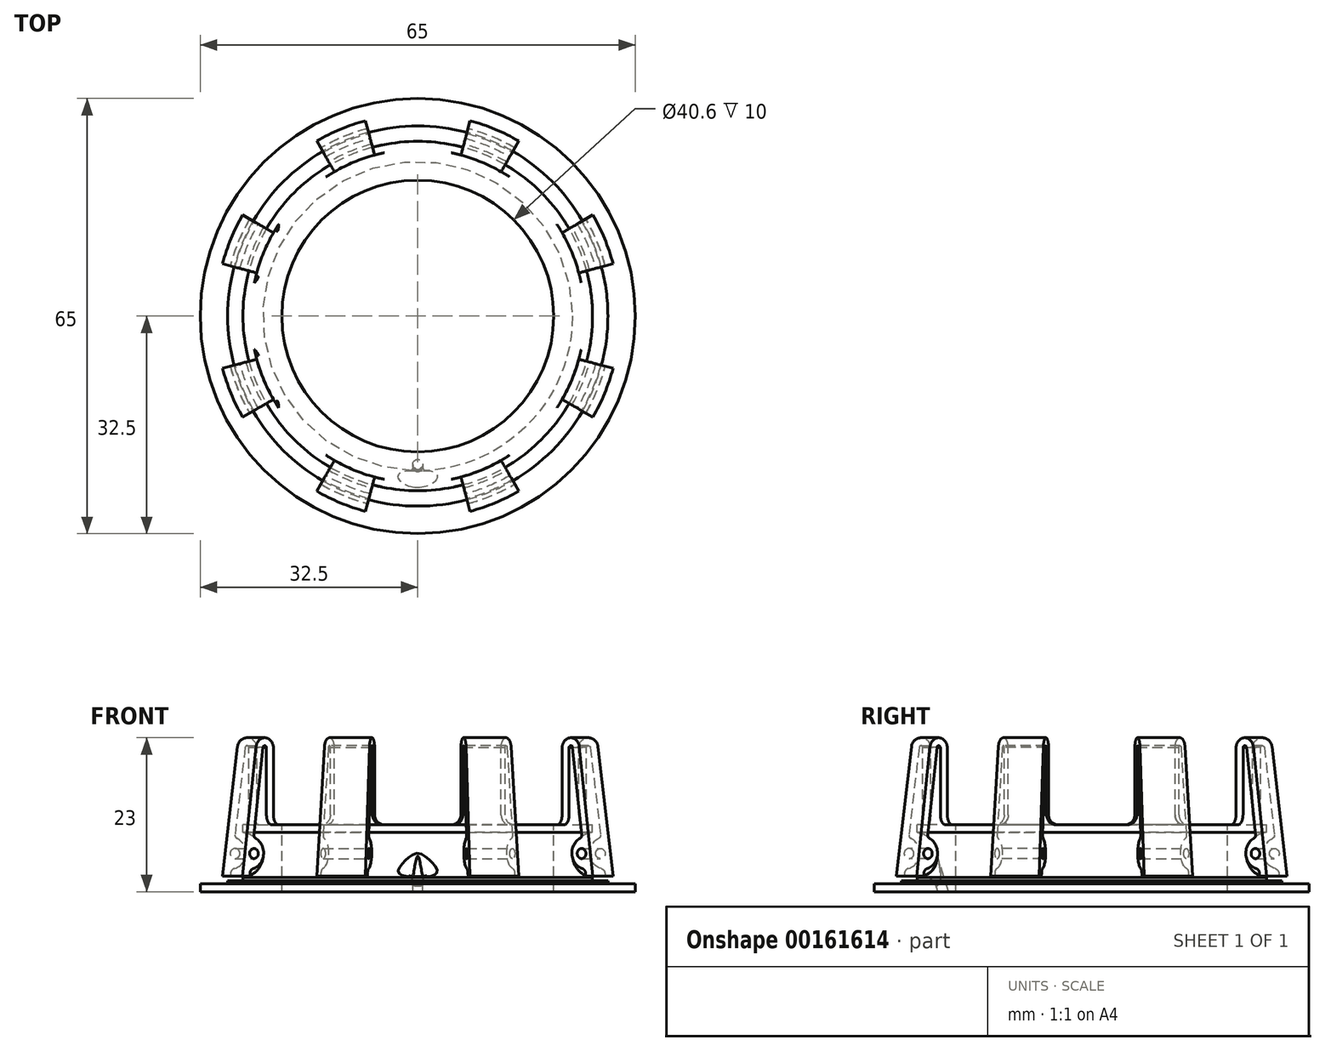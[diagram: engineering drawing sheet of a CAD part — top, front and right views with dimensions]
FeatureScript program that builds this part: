
annotation { "Feature Type Name" : "Feature", "Feature Type Description" : "" }
export const myFeature = defineFeature(function(context is Context, id is Id, definition is map)
    precondition{}
    {
        {
            var Q0;
            Q0=qCreatedBy(makeId("Front.planeOp"),FACE);
            var sketch = newSketch(context, id + "F0", { "sketchPlane" : qUnion([Q0])});
            skLineSegment(sketch, "E0", {"start": v(-32.5, 1.2) * mm, "end": v(-32.5, 0) * mm});
            skLineSegment(sketch, "E1", {"start": v(-32.5, 0) * mm, "end": v(-20.3, 0) * mm});
            skLineSegment(sketch, "E2", {"start": v(-32.5, 1.2) * mm, "end": v(-28.4, 1.2) * mm});
            skLineSegment(sketch, "E3", {"start": v(-28.4, 1.6) * mm, "end": v(-26.1, 1.6) * mm});
            skLineSegment(sketch, "E4", {"start": v(-20.3, 10) * mm, "end": v(-20.3, 0) * mm});
            skLineSegment(sketch, "E5", {"start": v(-20.3, 10) * mm, "end": v(0, 10) * mm, "construction": true});
            skLineSegment(sketch, "E6", {"start": v(0, 10) * mm, "end": v(0, 0) * mm, "construction": true});
            skLineSegment(sketch, "E7", {"start": v(0, 0) * mm, "end": v(-20.3, 0) * mm, "construction": true});
            skLineSegment(sketch, "E8", {"start": v(-29, 2.3) * mm, "end": v(-30.2, 2.3) * mm});
            skLineSegment(sketch, "E9", {"start": v(-30.2, 2.3) * mm, "end": v(-27.87, 21.69) * mm});
            skLineSegment(sketch, "E10", {"start": v(-29, 2.3) * mm, "end": v(-28.87, 3.4) * mm});
            skLineSegment(sketch, "E11", {"start": v(-26.1, 8.87) * mm, "end": v(-26.1, 21.58) * mm});
            skArc(sketch, "E12", {"start": v(-26.1, 21.58) * mm, "mid": v(-26.4, 21.8) * mm, "end": v(-26.69, 21.54) * mm});
            skLineSegment(sketch, "E13", {"start": v(-20.3, 10) * mm, "end": v(-24.9, 10) * mm});
            skLineSegment(sketch, "E14", {"start": v(-24.9, 10) * mm, "end": v(-24.9, 21.5) * mm});
            skArc(sketch, "E15", {"start": v(-24.9, 21.5) * mm, "mid": v(-26.3, 23) * mm, "end": v(-27.87, 21.69) * mm});
            skLineSegment(sketch, "E16", {"start": v(-28.4, 1.2) * mm, "end": v(-28.4, 1.6) * mm});
            skLineSegment(sketch, "E17", {"start": v(-26.1, 1.6) * mm, "end": v(-26.1, 2.11) * mm});
            skArc(sketch, "E18", {"start": v(-26.1, 2.11) * mm, "mid": v(-23.1, 5.49) * mm, "end": v(-26.1, 8.87) * mm});
            skArc(sketch, "E19", {"start": v(-28.87, 3.4) * mm, "mid": v(-26.6, 5.5) * mm, "end": v(-28.3, 8.1) * mm});
            skLineSegment(sketch, "E20.trimOffspring", {"start": v(-28.3, 8.1) * mm, "end": v(-26.69, 21.54) * mm});
            skCircle(sketch, "E21", {"center": v(-28.25, 5.7) * mm, "radius": 0.75 * mm, "construction": true});
            skLineSegment(sketch, "E22", {"start": v(-28.98, 5.79) * mm, "end": v(-28.25, 5.7) * mm, "construction": true});
            skLineSegment(sketch, "E23", {"start": v(-28.25, 5.7) * mm, "end": v(-26.5, 5.49) * mm, "construction": true});
            skSolve(sketch);
        }
        {
            var Q0;
            Q0=makeQuery(id+"F0.imprint","IMPRINT",FACE,{"disambiguationData":[TD([[makeQuery(id+"F0.imprint","IMPRINT",EDGE,{"derivedFrom":sQuery(id+"F0.wireOp",EDGE,"E0")}),1.0]])]});
            var Q1;
            Q1=sQuery(id+"F0.wireOp",EDGE,"E6");
            revolve(context, id + "F1", {"entities" : qUnion([Q0]), "axis" : qUnion([Q1]), "revolveType" : RevolveType.FULL});
        }
        {
            var Q0;
            Q0=qCreatedBy(makeId("Front.planeOp"),FACE);
            var sketch = newSketch(context, id + "F2", { "sketchPlane" : qUnion([Q0])});
            skCircle(sketch, "E24", {"center": v(-28.25, 5.7) * mm, "radius": 0.75 * mm});
            skSolve(sketch);
        }
        {
            var Q0;
            Q0 = qSketchRegion(id + "F2", true);
            var Q1;
            Q1=sQuery(id+"F0.wireOp",EDGE,"E6");
            revolve(context, id + "F3", {"operationType" : NewBodyOperationType.REMOVE, "entities" : qUnion([Q0]), "axis" : qUnion([Q1]), "revolveType" : RevolveType.FULL, "oppositeDirection" : true});
        }
        {
            var Q0;
            Q0=qCreatedBy(makeId("Front.planeOp"),FACE);
            var sketch = newSketch(context, id + "F4", { "sketchPlane" : qUnion([Q0])});
            skLineSegment(sketch, "E25", {"start": v(-33, 1.7) * mm, "end": v(-26.1, 1.7) * mm});
            skLineSegment(sketch, "E26", {"start": v(-26.1, 1.7) * mm, "end": v(-26.1, 10) * mm});
            skLineSegment(sketch, "E27", {"start": v(-26.1, 10) * mm, "end": v(0, 10) * mm});
            skLineSegment(sketch, "E28", {"start": v(0, 26) * mm, "end": v(0, 10) * mm});
            skLineSegment(sketch, "E29", {"start": v(0, 26) * mm, "end": v(-33, 26) * mm});
            skLineSegment(sketch, "E30", {"start": v(-33, 1.7) * mm, "end": v(-33, 26) * mm});
            skSolve(sketch);
        }
        {
            var Q0;
            Q0=makeQuery(id+"F4.imprint","IMPRINT",FACE,{"disambiguationData":[TD([[makeQuery(id+"F4.imprint","IMPRINT",EDGE,{"derivedFrom":sQuery(id+"F4.wireOp",EDGE,"E25")}),1.0]])]});
            var Q1;
            Q1=sQuery(id+"F4.wireOp",EDGE,"E28");
            revolve(context, id + "F5", {"entities" : qUnion([Q0]), "axis" : qUnion([Q1]), "revolveType" : RevolveType.SYMMETRIC, "oppositeDirection" : true, "angle" : 30 * degree});
        }
        {
            var Q0;
            Q0=makeQuery(id+"F5.opRevolve","SWEPT_BODY",BODY,{"disambiguationData":[OSD([sQuery(id+"F4.wireOp",EDGE,"E25"),sQuery(id+"F4.wireOp",EDGE,"E26"),sQuery(id+"F4.wireOp",EDGE,"E27"),sQuery(id+"F4.wireOp",EDGE,"E28"),sQuery(id+"F4.wireOp",EDGE,"E29"),sQuery(id+"F4.wireOp",EDGE,"E30")])]});
            var Q1;
            Q1=makeQuery(id+"F5.opRevolve","CAP_EDGE",EDGE,{"disambiguationData":[OSD([sQuery(id+"F4.wireOp",EDGE,"E28")])],"isStart":true});
            circularPattern(context, id + "F6", {"entities" : qUnion([Q0]), "axis" : qUnion([Q1]), "angle" : 360 * degree, "instanceCount" : 8, "equalSpace" : true});
        }
        {
            var Q0;
            Q0=makeQuery(id+"F5.opRevolve","SWEPT_BODY",BODY,{"disambiguationData":[OSD([sQuery(id+"F4.wireOp",EDGE,"E25"),sQuery(id+"F4.wireOp",EDGE,"E26"),sQuery(id+"F4.wireOp",EDGE,"E27"),sQuery(id+"F4.wireOp",EDGE,"E28"),sQuery(id+"F4.wireOp",EDGE,"E29"),sQuery(id+"F4.wireOp",EDGE,"E30")])]});
            var Q1;
            Q1=makeQuery(id+"F6.opPattern","COPY",BODY,{"derivedFrom":makeQuery(id+"F5.opRevolve","SWEPT_BODY",BODY,{"disambiguationData":[OSD([sQuery(id+"F4.wireOp",EDGE,"E25"),sQuery(id+"F4.wireOp",EDGE,"E26"),sQuery(id+"F4.wireOp",EDGE,"E27"),sQuery(id+"F4.wireOp",EDGE,"E28"),sQuery(id+"F4.wireOp",EDGE,"E29"),sQuery(id+"F4.wireOp",EDGE,"E30")])]}),"instanceName":"1"});
            var Q2;
            Q2=makeQuery(id+"F6.opPattern","COPY",BODY,{"derivedFrom":makeQuery(id+"F5.opRevolve","SWEPT_BODY",BODY,{"disambiguationData":[OSD([sQuery(id+"F4.wireOp",EDGE,"E25"),sQuery(id+"F4.wireOp",EDGE,"E26"),sQuery(id+"F4.wireOp",EDGE,"E27"),sQuery(id+"F4.wireOp",EDGE,"E28"),sQuery(id+"F4.wireOp",EDGE,"E29"),sQuery(id+"F4.wireOp",EDGE,"E30")])]}),"instanceName":"2"});
            var Q3;
            Q3=makeQuery(id+"F6.opPattern","COPY",BODY,{"derivedFrom":makeQuery(id+"F5.opRevolve","SWEPT_BODY",BODY,{"disambiguationData":[OSD([sQuery(id+"F4.wireOp",EDGE,"E25"),sQuery(id+"F4.wireOp",EDGE,"E26"),sQuery(id+"F4.wireOp",EDGE,"E27"),sQuery(id+"F4.wireOp",EDGE,"E28"),sQuery(id+"F4.wireOp",EDGE,"E29"),sQuery(id+"F4.wireOp",EDGE,"E30")])]}),"instanceName":"3"});
            var Q4;
            Q4=makeQuery(id+"F6.opPattern","COPY",BODY,{"derivedFrom":makeQuery(id+"F5.opRevolve","SWEPT_BODY",BODY,{"disambiguationData":[OSD([sQuery(id+"F4.wireOp",EDGE,"E25"),sQuery(id+"F4.wireOp",EDGE,"E26"),sQuery(id+"F4.wireOp",EDGE,"E27"),sQuery(id+"F4.wireOp",EDGE,"E28"),sQuery(id+"F4.wireOp",EDGE,"E29"),sQuery(id+"F4.wireOp",EDGE,"E30")])]}),"instanceName":"4"});
            var Q5;
            Q5=makeQuery(id+"F6.opPattern","COPY",BODY,{"derivedFrom":makeQuery(id+"F5.opRevolve","SWEPT_BODY",BODY,{"disambiguationData":[OSD([sQuery(id+"F4.wireOp",EDGE,"E25"),sQuery(id+"F4.wireOp",EDGE,"E26"),sQuery(id+"F4.wireOp",EDGE,"E27"),sQuery(id+"F4.wireOp",EDGE,"E28"),sQuery(id+"F4.wireOp",EDGE,"E29"),sQuery(id+"F4.wireOp",EDGE,"E30")])]}),"instanceName":"5"});
            var Q6;
            Q6=makeQuery(id+"F6.opPattern","COPY",BODY,{"derivedFrom":makeQuery(id+"F5.opRevolve","SWEPT_BODY",BODY,{"disambiguationData":[OSD([sQuery(id+"F4.wireOp",EDGE,"E25"),sQuery(id+"F4.wireOp",EDGE,"E26"),sQuery(id+"F4.wireOp",EDGE,"E27"),sQuery(id+"F4.wireOp",EDGE,"E28"),sQuery(id+"F4.wireOp",EDGE,"E29"),sQuery(id+"F4.wireOp",EDGE,"E30")])]}),"instanceName":"6"});
            var Q7;
            Q7=makeQuery(id+"F6.opPattern","COPY",BODY,{"derivedFrom":makeQuery(id+"F5.opRevolve","SWEPT_BODY",BODY,{"disambiguationData":[OSD([sQuery(id+"F4.wireOp",EDGE,"E25"),sQuery(id+"F4.wireOp",EDGE,"E26"),sQuery(id+"F4.wireOp",EDGE,"E27"),sQuery(id+"F4.wireOp",EDGE,"E28"),sQuery(id+"F4.wireOp",EDGE,"E29"),sQuery(id+"F4.wireOp",EDGE,"E30")])]}),"instanceName":"7"});
            var Q8;
            Q8=makeQuery(id+"F1.opRevolve","SWEPT_BODY",BODY,{"disambiguationData":[OSD([sQuery(id+"F0.wireOp",EDGE,"E0"),sQuery(id+"F0.wireOp",EDGE,"E1"),sQuery(id+"F0.wireOp",EDGE,"E2"),sQuery(id+"F0.wireOp",EDGE,"E3"),sQuery(id+"F0.wireOp",EDGE,"E4"),sQuery(id+"F0.wireOp",EDGE,"E8"),sQuery(id+"F0.wireOp",EDGE,"E9"),sQuery(id+"F0.wireOp",EDGE,"E10"),sQuery(id+"F0.wireOp",EDGE,"E11"),sQuery(id+"F0.wireOp",EDGE,"E12"),sQuery(id+"F0.wireOp",EDGE,"E13"),sQuery(id+"F0.wireOp",EDGE,"E14"),sQuery(id+"F0.wireOp",EDGE,"E15"),sQuery(id+"F0.wireOp",EDGE,"E16"),sQuery(id+"F0.wireOp",EDGE,"E17"),sQuery(id+"F0.wireOp",EDGE,"E18"),sQuery(id+"F0.wireOp",EDGE,"E19"),sQuery(id+"F0.wireOp",EDGE,"E20.trimOffspring")])]});
            booleanBodies(context, id + "F7", {"operationType" : BooleanOperationType.SUBTRACTION, "tools" : qUnion([Q0, Q1, Q2, Q3, Q4, Q5, Q6, Q7]), "targets" : qUnion([Q8])});
        }
        {
            var Q0;
            Q0=qCreatedBy(makeId("Right.planeOp"),FACE);
            var sketch = newSketch(context, id + "F8", { "sketchPlane" : qUnion([Q0])});
            skLineSegment(sketch, "E31", {"start": v(-23.3, 6.22) * mm, "end": v(-21.4, 0) * mm});
            skLineSegment(sketch, "E32", {"start": v(-21.4, 0) * mm, "end": v(-22.12, -0.22) * mm});
            skLineSegment(sketch, "E33", {"start": v(-22.12, -0.22) * mm, "end": v(-24.02, 6) * mm});
            skLineSegment(sketch, "E34", {"start": v(-23.3, 6.22) * mm, "end": v(-24.02, 6) * mm});
            skSolve(sketch);
        }
        {
            var Q0;
            Q0 = qSketchRegion(id + "F8", true);
            var Q1;
            Q1=sQuery(id+"F8.wireOp",EDGE,"E33");
            revolve(context, id + "F9", {"operationType" : NewBodyOperationType.REMOVE, "entities" : qUnion([Q0]), "axis" : qUnion([Q1]), "revolveType" : RevolveType.FULL, "oppositeDirection" : true});
        }
        {
            var Q0;
            Q0=makeQuery(id+"F9.boolean.opBoolean","INTERSECT",EDGE,{"derivedFrom":[makeQuery(id+"F1.opRevolve","SWEPT_FACE",FACE,{"disambiguationData":[OSD([sQuery(id+"F0.wireOp",EDGE,"E18")])]}),makeQuery(id+"F9.opRevolve","SWEPT_FACE",FACE,{"disambiguationData":[OSD([sQuery(id+"F8.wireOp",EDGE,"E31")])]})]});
            fillet(context, id + "F10", {"entities" : qUnion([Q0]), "radius" : 2 * mm, "tangentPropagation" : true, "allowEdgeOverflow" : false});
        }
        {
            var Q0;
            {var subQ0=sQuery(id+"F0.wireOp",EDGE,"E10");var subQ1=sQuery(id+"F4.wireOp",EDGE,"E30");var subQ2=sQuery(id+"F4.wireOp",EDGE,"E29");var subQ3=sQuery(id+"F4.wireOp",EDGE,"E28");var subQ4=sQuery(id+"F4.wireOp",EDGE,"E27");var subQ5=sQuery(id+"F4.wireOp",EDGE,"E26");var subQ6=sQuery(id+"F4.wireOp",EDGE,"E25");var subQ7=sQuery(id+"F0.wireOp",EDGE,"E19");Q0=makeQuery(id+"F7.opBoolean","SPLIT",EDGE,{"disambiguationData":[TD([makeQuery(id+"F6.opPattern","COPY",FACE,{"derivedFrom":makeQuery(id+"F5.opRevolve","CAP_FACE",FACE,{"disambiguationData":[OSD([subQ6,subQ5,subQ4,subQ3,subQ2,subQ1])],"isStart":true}),"instanceName":"6"})])],"derivedFrom":makeQuery(id+"F1.opRevolve","SWEPT_EDGE",EDGE,{"disambiguationData":[OSD([subQ0,subQ7])]})});}
            var Q1;
            {var subQ0=sQuery(id+"F0.wireOp",EDGE,"E10");var subQ1=sQuery(id+"F4.wireOp",EDGE,"E30");var subQ2=sQuery(id+"F4.wireOp",EDGE,"E29");var subQ3=sQuery(id+"F4.wireOp",EDGE,"E28");var subQ4=sQuery(id+"F4.wireOp",EDGE,"E27");var subQ5=sQuery(id+"F4.wireOp",EDGE,"E26");var subQ6=sQuery(id+"F4.wireOp",EDGE,"E25");var subQ7=sQuery(id+"F0.wireOp",EDGE,"E19");Q1=makeQuery(id+"F7.opBoolean","SPLIT",EDGE,{"disambiguationData":[TD([makeQuery(id+"F6.opPattern","COPY",FACE,{"derivedFrom":makeQuery(id+"F5.opRevolve","CAP_FACE",FACE,{"disambiguationData":[OSD([subQ6,subQ5,subQ4,subQ3,subQ2,subQ1])],"isStart":true}),"instanceName":"5"})])],"derivedFrom":makeQuery(id+"F1.opRevolve","SWEPT_EDGE",EDGE,{"disambiguationData":[OSD([subQ0,subQ7])]})});}
            var Q2;
            {var subQ0=sQuery(id+"F0.wireOp",EDGE,"E10");var subQ1=sQuery(id+"F0.wireOp",EDGE,"E19");var subQ2=sQuery(id+"F4.wireOp",EDGE,"E30");var subQ3=sQuery(id+"F4.wireOp",EDGE,"E29");var subQ4=sQuery(id+"F4.wireOp",EDGE,"E28");var subQ5=sQuery(id+"F4.wireOp",EDGE,"E27");var subQ6=sQuery(id+"F4.wireOp",EDGE,"E26");var subQ7=sQuery(id+"F4.wireOp",EDGE,"E25");Q2=makeQuery(id+"F7.opBoolean","SPLIT",EDGE,{"disambiguationData":[TD([makeQuery(id+"F6.opPattern","COPY",FACE,{"derivedFrom":makeQuery(id+"F5.opRevolve","CAP_FACE",FACE,{"disambiguationData":[OSD([subQ7,subQ6,subQ5,subQ4,subQ3,subQ2])],"isStart":true}),"instanceName":"4"})])],"derivedFrom":makeQuery(id+"F1.opRevolve","SWEPT_EDGE",EDGE,{"disambiguationData":[OSD([subQ0,subQ1])]})});}
            var Q3;
            {var subQ0=sQuery(id+"F0.wireOp",EDGE,"E10");var subQ1=sQuery(id+"F0.wireOp",EDGE,"E19");var subQ2=sQuery(id+"F4.wireOp",EDGE,"E30");var subQ3=sQuery(id+"F4.wireOp",EDGE,"E29");var subQ4=sQuery(id+"F4.wireOp",EDGE,"E28");var subQ5=sQuery(id+"F4.wireOp",EDGE,"E27");var subQ6=sQuery(id+"F4.wireOp",EDGE,"E26");var subQ7=sQuery(id+"F4.wireOp",EDGE,"E25");Q3=makeQuery(id+"F7.opBoolean","SPLIT",EDGE,{"disambiguationData":[TD([makeQuery(id+"F6.opPattern","COPY",FACE,{"derivedFrom":makeQuery(id+"F5.opRevolve","CAP_FACE",FACE,{"disambiguationData":[OSD([subQ7,subQ6,subQ5,subQ4,subQ3,subQ2])],"isStart":true}),"instanceName":"3"})])],"derivedFrom":makeQuery(id+"F1.opRevolve","SWEPT_EDGE",EDGE,{"disambiguationData":[OSD([subQ0,subQ1])]})});}
            var Q4;
            {var subQ0=sQuery(id+"F0.wireOp",EDGE,"E10");var subQ1=sQuery(id+"F0.wireOp",EDGE,"E19");var subQ2=sQuery(id+"F4.wireOp",EDGE,"E30");var subQ3=sQuery(id+"F4.wireOp",EDGE,"E29");var subQ4=sQuery(id+"F4.wireOp",EDGE,"E28");var subQ5=sQuery(id+"F4.wireOp",EDGE,"E27");var subQ6=sQuery(id+"F4.wireOp",EDGE,"E26");var subQ7=sQuery(id+"F4.wireOp",EDGE,"E25");Q4=makeQuery(id+"F7.opBoolean","SPLIT",EDGE,{"disambiguationData":[TD([makeQuery(id+"F6.opPattern","COPY",FACE,{"derivedFrom":makeQuery(id+"F5.opRevolve","CAP_FACE",FACE,{"disambiguationData":[OSD([subQ7,subQ6,subQ5,subQ4,subQ3,subQ2])],"isStart":true}),"instanceName":"2"})])],"derivedFrom":makeQuery(id+"F1.opRevolve","SWEPT_EDGE",EDGE,{"disambiguationData":[OSD([subQ0,subQ1])]})});}
            var Q5;
            {var subQ0=sQuery(id+"F0.wireOp",EDGE,"E10");var subQ1=sQuery(id+"F4.wireOp",EDGE,"E30");var subQ2=sQuery(id+"F4.wireOp",EDGE,"E29");var subQ3=sQuery(id+"F4.wireOp",EDGE,"E28");var subQ4=sQuery(id+"F4.wireOp",EDGE,"E27");var subQ5=sQuery(id+"F4.wireOp",EDGE,"E26");var subQ6=sQuery(id+"F4.wireOp",EDGE,"E25");var subQ7=sQuery(id+"F0.wireOp",EDGE,"E19");Q5=makeQuery(id+"F7.opBoolean","SPLIT",EDGE,{"disambiguationData":[TD([makeQuery(id+"F6.opPattern","COPY",FACE,{"derivedFrom":makeQuery(id+"F5.opRevolve","CAP_FACE",FACE,{"disambiguationData":[OSD([subQ6,subQ5,subQ4,subQ3,subQ2,subQ1])],"isStart":true}),"instanceName":"1"})])],"derivedFrom":makeQuery(id+"F1.opRevolve","SWEPT_EDGE",EDGE,{"disambiguationData":[OSD([subQ0,subQ7])]})});}
            var Q6;
            {var subQ0=sQuery(id+"F0.wireOp",EDGE,"E10");var subQ1=sQuery(id+"F0.wireOp",EDGE,"E19");var subQ2=sQuery(id+"F4.wireOp",EDGE,"E30");var subQ3=sQuery(id+"F4.wireOp",EDGE,"E29");var subQ4=sQuery(id+"F4.wireOp",EDGE,"E28");var subQ5=sQuery(id+"F4.wireOp",EDGE,"E27");var subQ6=sQuery(id+"F4.wireOp",EDGE,"E26");var subQ7=sQuery(id+"F4.wireOp",EDGE,"E25");Q6=makeQuery(id+"F7.opBoolean","SPLIT",EDGE,{"disambiguationData":[TD([makeQuery(id+"F5.opRevolve","CAP_FACE",FACE,{"disambiguationData":[OSD([subQ7,subQ6,subQ5,subQ4,subQ3,subQ2])],"isStart":true})])],"derivedFrom":makeQuery(id+"F1.opRevolve","SWEPT_EDGE",EDGE,{"disambiguationData":[OSD([subQ0,subQ1])]})});}
            var Q7;
            {var subQ0=sQuery(id+"F0.wireOp",EDGE,"E10");var subQ1=sQuery(id+"F0.wireOp",EDGE,"E19");var subQ2=sQuery(id+"F4.wireOp",EDGE,"E30");var subQ3=sQuery(id+"F4.wireOp",EDGE,"E29");var subQ4=sQuery(id+"F4.wireOp",EDGE,"E28");var subQ5=sQuery(id+"F4.wireOp",EDGE,"E27");var subQ6=sQuery(id+"F4.wireOp",EDGE,"E26");var subQ7=sQuery(id+"F4.wireOp",EDGE,"E25");Q7=makeQuery(id+"F7.opBoolean","SPLIT",EDGE,{"disambiguationData":[TD([makeQuery(id+"F5.opRevolve","CAP_FACE",FACE,{"disambiguationData":[OSD([subQ7,subQ6,subQ5,subQ4,subQ3,subQ2])],"isStart":false})])],"derivedFrom":makeQuery(id+"F1.opRevolve","SWEPT_EDGE",EDGE,{"disambiguationData":[OSD([subQ0,subQ1])]})});}
            fillet(context, id + "F11", {"entities" : qUnion([Q0, Q1, Q2, Q3, Q4, Q5, Q6, Q7]), "radius" : .8 * mm, "tangentPropagation" : true, "allowEdgeOverflow" : false});
        }
        {
            var Q0;
            Q0=makeQuery(id+"F7.opBoolean","COPY",EDGE,{"derivedFrom":makeQuery(id+"F6.opPattern","COPY",EDGE,{"derivedFrom":makeQuery(id+"F5.opRevolve","CAP_EDGE",EDGE,{"disambiguationData":[OSD([sQuery(id+"F4.wireOp",EDGE,"E27")])],"isStart":true}),"instanceName":"5"})});
            var Q1;
            Q1=makeQuery(id+"F7.opBoolean","COPY",EDGE,{"derivedFrom":makeQuery(id+"F6.opPattern","COPY",EDGE,{"derivedFrom":makeQuery(id+"F5.opRevolve","CAP_EDGE",EDGE,{"disambiguationData":[OSD([sQuery(id+"F4.wireOp",EDGE,"E27")])],"isStart":false}),"instanceName":"6"})});
            var Q2;
            Q2=makeQuery(id+"F7.opBoolean","COPY",EDGE,{"derivedFrom":makeQuery(id+"F6.opPattern","COPY",EDGE,{"derivedFrom":makeQuery(id+"F5.opRevolve","CAP_EDGE",EDGE,{"disambiguationData":[OSD([sQuery(id+"F4.wireOp",EDGE,"E27")])],"isStart":true}),"instanceName":"6"})});
            var Q3;
            Q3=makeQuery(id+"F7.opBoolean","COPY",EDGE,{"derivedFrom":makeQuery(id+"F6.opPattern","COPY",EDGE,{"derivedFrom":makeQuery(id+"F5.opRevolve","CAP_EDGE",EDGE,{"disambiguationData":[OSD([sQuery(id+"F4.wireOp",EDGE,"E27")])],"isStart":false}),"instanceName":"7"})});
            var Q4;
            Q4=makeQuery(id+"F7.opBoolean","COPY",EDGE,{"derivedFrom":makeQuery(id+"F5.opRevolve","CAP_EDGE",EDGE,{"disambiguationData":[OSD([sQuery(id+"F4.wireOp",EDGE,"E27")])],"isStart":false})});
            var Q5;
            Q5=makeQuery(id+"F7.opBoolean","COPY",EDGE,{"derivedFrom":makeQuery(id+"F6.opPattern","COPY",EDGE,{"derivedFrom":makeQuery(id+"F5.opRevolve","CAP_EDGE",EDGE,{"disambiguationData":[OSD([sQuery(id+"F4.wireOp",EDGE,"E27")])],"isStart":true}),"instanceName":"7"})});
            var Q6;
            Q6=makeQuery(id+"F7.opBoolean","COPY",EDGE,{"derivedFrom":makeQuery(id+"F5.opRevolve","CAP_EDGE",EDGE,{"disambiguationData":[OSD([sQuery(id+"F4.wireOp",EDGE,"E27")])],"isStart":true})});
            var Q7;
            Q7=makeQuery(id+"F7.opBoolean","COPY",EDGE,{"derivedFrom":makeQuery(id+"F6.opPattern","COPY",EDGE,{"derivedFrom":makeQuery(id+"F5.opRevolve","CAP_EDGE",EDGE,{"disambiguationData":[OSD([sQuery(id+"F4.wireOp",EDGE,"E27")])],"isStart":false}),"instanceName":"1"})});
            var Q8;
            Q8=makeQuery(id+"F7.opBoolean","COPY",EDGE,{"derivedFrom":makeQuery(id+"F6.opPattern","COPY",EDGE,{"derivedFrom":makeQuery(id+"F5.opRevolve","CAP_EDGE",EDGE,{"disambiguationData":[OSD([sQuery(id+"F4.wireOp",EDGE,"E27")])],"isStart":true}),"instanceName":"1"})});
            var Q9;
            Q9=makeQuery(id+"F7.opBoolean","COPY",EDGE,{"derivedFrom":makeQuery(id+"F6.opPattern","COPY",EDGE,{"derivedFrom":makeQuery(id+"F5.opRevolve","CAP_EDGE",EDGE,{"disambiguationData":[OSD([sQuery(id+"F4.wireOp",EDGE,"E27")])],"isStart":false}),"instanceName":"2"})});
            var Q10;
            Q10=makeQuery(id+"F7.opBoolean","COPY",EDGE,{"derivedFrom":makeQuery(id+"F6.opPattern","COPY",EDGE,{"derivedFrom":makeQuery(id+"F5.opRevolve","CAP_EDGE",EDGE,{"disambiguationData":[OSD([sQuery(id+"F4.wireOp",EDGE,"E27")])],"isStart":true}),"instanceName":"2"})});
            var Q11;
            Q11=makeQuery(id+"F7.opBoolean","COPY",EDGE,{"derivedFrom":makeQuery(id+"F6.opPattern","COPY",EDGE,{"derivedFrom":makeQuery(id+"F5.opRevolve","CAP_EDGE",EDGE,{"disambiguationData":[OSD([sQuery(id+"F4.wireOp",EDGE,"E27")])],"isStart":false}),"instanceName":"3"})});
            var Q12;
            Q12=makeQuery(id+"F7.opBoolean","COPY",EDGE,{"derivedFrom":makeQuery(id+"F6.opPattern","COPY",EDGE,{"derivedFrom":makeQuery(id+"F5.opRevolve","CAP_EDGE",EDGE,{"disambiguationData":[OSD([sQuery(id+"F4.wireOp",EDGE,"E27")])],"isStart":false}),"instanceName":"4"})});
            var Q13;
            Q13=makeQuery(id+"F7.opBoolean","COPY",EDGE,{"derivedFrom":makeQuery(id+"F6.opPattern","COPY",EDGE,{"derivedFrom":makeQuery(id+"F5.opRevolve","CAP_EDGE",EDGE,{"disambiguationData":[OSD([sQuery(id+"F4.wireOp",EDGE,"E27")])],"isStart":true}),"instanceName":"3"})});
            var Q14;
            Q14=makeQuery(id+"F7.opBoolean","COPY",EDGE,{"derivedFrom":makeQuery(id+"F6.opPattern","COPY",EDGE,{"derivedFrom":makeQuery(id+"F5.opRevolve","CAP_EDGE",EDGE,{"disambiguationData":[OSD([sQuery(id+"F4.wireOp",EDGE,"E27")])],"isStart":true}),"instanceName":"4"})});
            var Q15;
            Q15=makeQuery(id+"F7.opBoolean","COPY",EDGE,{"derivedFrom":makeQuery(id+"F6.opPattern","COPY",EDGE,{"derivedFrom":makeQuery(id+"F5.opRevolve","CAP_EDGE",EDGE,{"disambiguationData":[OSD([sQuery(id+"F4.wireOp",EDGE,"E27")])],"isStart":false}),"instanceName":"5"})});
            fillet(context, id + "F12", {"entities" : qUnion([Q0, Q1, Q2, Q3, Q4, Q5, Q6, Q7, Q8, Q9, Q10, Q11, Q12, Q13, Q14, Q15]), "radius" : 1.5 * mm, "tangentPropagation" : true, "allowEdgeOverflow" : false});
        }
        {
            var Q0;
            {var subQ0=sQuery(id+"F4.wireOp",EDGE,"E27");var subQ2=sQuery(id+"F4.wireOp",EDGE,"E30");var subQ3=sQuery(id+"F4.wireOp",EDGE,"E29");var subQ4=sQuery(id+"F4.wireOp",EDGE,"E28");var subQ5=sQuery(id+"F4.wireOp",EDGE,"E26");var subQ6=sQuery(id+"F4.wireOp",EDGE,"E25");var subQ7=sQuery(id+"F0.wireOp",EDGE,"E14");var subQ8=sQuery(id+"F0.wireOp",EDGE,"E13");Q0=makeQuery(id+"F7.opBoolean","SPLIT",EDGE,{"disambiguationData":[TD([makeQuery(id+"F6.opPattern","COPY",FACE,{"derivedFrom":makeQuery(id+"F5.opRevolve","CAP_FACE",FACE,{"disambiguationData":[OSD([subQ6,subQ5,subQ0,subQ4,subQ3,subQ2])],"isStart":true}),"instanceName":"5"})])],"derivedFrom":makeQuery(id+"F1.opRevolve","SWEPT_EDGE",EDGE,{"disambiguationData":[OSD([subQ8,subQ7])]})});}
            var Q1;
            {var subQ0=sQuery(id+"F4.wireOp",EDGE,"E27");var subQ2=sQuery(id+"F4.wireOp",EDGE,"E30");var subQ3=sQuery(id+"F4.wireOp",EDGE,"E29");var subQ4=sQuery(id+"F4.wireOp",EDGE,"E28");var subQ5=sQuery(id+"F4.wireOp",EDGE,"E26");var subQ6=sQuery(id+"F4.wireOp",EDGE,"E25");var subQ7=sQuery(id+"F0.wireOp",EDGE,"E13");var subQ8=sQuery(id+"F0.wireOp",EDGE,"E14");Q1=makeQuery(id+"F7.opBoolean","SPLIT",EDGE,{"disambiguationData":[TD([makeQuery(id+"F6.opPattern","COPY",FACE,{"derivedFrom":makeQuery(id+"F5.opRevolve","CAP_FACE",FACE,{"disambiguationData":[OSD([subQ6,subQ5,subQ0,subQ4,subQ3,subQ2])],"isStart":true}),"instanceName":"4"})])],"derivedFrom":makeQuery(id+"F1.opRevolve","SWEPT_EDGE",EDGE,{"disambiguationData":[OSD([subQ7,subQ8])]})});}
            var Q2;
            {var subQ0=sQuery(id+"F4.wireOp",EDGE,"E27");var subQ2=sQuery(id+"F4.wireOp",EDGE,"E30");var subQ3=sQuery(id+"F4.wireOp",EDGE,"E29");var subQ4=sQuery(id+"F4.wireOp",EDGE,"E28");var subQ5=sQuery(id+"F4.wireOp",EDGE,"E26");var subQ6=sQuery(id+"F4.wireOp",EDGE,"E25");var subQ7=sQuery(id+"F0.wireOp",EDGE,"E14");var subQ8=sQuery(id+"F0.wireOp",EDGE,"E13");Q2=makeQuery(id+"F7.opBoolean","SPLIT",EDGE,{"disambiguationData":[TD([makeQuery(id+"F6.opPattern","COPY",FACE,{"derivedFrom":makeQuery(id+"F5.opRevolve","CAP_FACE",FACE,{"disambiguationData":[OSD([subQ6,subQ5,subQ0,subQ4,subQ3,subQ2])],"isStart":true}),"instanceName":"3"})])],"derivedFrom":makeQuery(id+"F1.opRevolve","SWEPT_EDGE",EDGE,{"disambiguationData":[OSD([subQ8,subQ7])]})});}
            var Q3;
            {var subQ0=sQuery(id+"F4.wireOp",EDGE,"E27");var subQ2=sQuery(id+"F4.wireOp",EDGE,"E30");var subQ3=sQuery(id+"F4.wireOp",EDGE,"E29");var subQ4=sQuery(id+"F4.wireOp",EDGE,"E28");var subQ5=sQuery(id+"F4.wireOp",EDGE,"E26");var subQ6=sQuery(id+"F4.wireOp",EDGE,"E25");var subQ7=sQuery(id+"F0.wireOp",EDGE,"E14");var subQ8=sQuery(id+"F0.wireOp",EDGE,"E13");Q3=makeQuery(id+"F7.opBoolean","SPLIT",EDGE,{"disambiguationData":[TD([makeQuery(id+"F6.opPattern","COPY",FACE,{"derivedFrom":makeQuery(id+"F5.opRevolve","CAP_FACE",FACE,{"disambiguationData":[OSD([subQ6,subQ5,subQ0,subQ4,subQ3,subQ2])],"isStart":true}),"instanceName":"2"})])],"derivedFrom":makeQuery(id+"F1.opRevolve","SWEPT_EDGE",EDGE,{"disambiguationData":[OSD([subQ8,subQ7])]})});}
            var Q4;
            {var subQ0=sQuery(id+"F4.wireOp",EDGE,"E27");var subQ2=sQuery(id+"F4.wireOp",EDGE,"E30");var subQ3=sQuery(id+"F4.wireOp",EDGE,"E29");var subQ4=sQuery(id+"F4.wireOp",EDGE,"E28");var subQ5=sQuery(id+"F4.wireOp",EDGE,"E26");var subQ6=sQuery(id+"F4.wireOp",EDGE,"E25");var subQ7=sQuery(id+"F0.wireOp",EDGE,"E13");var subQ8=sQuery(id+"F0.wireOp",EDGE,"E14");Q4=makeQuery(id+"F7.opBoolean","SPLIT",EDGE,{"disambiguationData":[TD([makeQuery(id+"F6.opPattern","COPY",FACE,{"derivedFrom":makeQuery(id+"F5.opRevolve","CAP_FACE",FACE,{"disambiguationData":[OSD([subQ6,subQ5,subQ0,subQ4,subQ3,subQ2])],"isStart":true}),"instanceName":"1"})])],"derivedFrom":makeQuery(id+"F1.opRevolve","SWEPT_EDGE",EDGE,{"disambiguationData":[OSD([subQ7,subQ8])]})});}
            var Q5;
            {var subQ0=sQuery(id+"F4.wireOp",EDGE,"E27");var subQ2=sQuery(id+"F4.wireOp",EDGE,"E30");var subQ3=sQuery(id+"F4.wireOp",EDGE,"E29");var subQ4=sQuery(id+"F4.wireOp",EDGE,"E28");var subQ5=sQuery(id+"F4.wireOp",EDGE,"E26");var subQ6=sQuery(id+"F4.wireOp",EDGE,"E25");var subQ7=sQuery(id+"F0.wireOp",EDGE,"E14");var subQ8=sQuery(id+"F0.wireOp",EDGE,"E13");Q5=makeQuery(id+"F7.opBoolean","SPLIT",EDGE,{"disambiguationData":[TD([makeQuery(id+"F5.opRevolve","CAP_FACE",FACE,{"disambiguationData":[OSD([subQ6,subQ5,subQ0,subQ4,subQ3,subQ2])],"isStart":true})])],"derivedFrom":makeQuery(id+"F1.opRevolve","SWEPT_EDGE",EDGE,{"disambiguationData":[OSD([subQ8,subQ7])]})});}
            var Q6;
            {var subQ0=sQuery(id+"F4.wireOp",EDGE,"E27");var subQ2=sQuery(id+"F4.wireOp",EDGE,"E30");var subQ3=sQuery(id+"F4.wireOp",EDGE,"E29");var subQ4=sQuery(id+"F4.wireOp",EDGE,"E28");var subQ5=sQuery(id+"F4.wireOp",EDGE,"E26");var subQ6=sQuery(id+"F4.wireOp",EDGE,"E25");var subQ7=sQuery(id+"F0.wireOp",EDGE,"E14");var subQ8=sQuery(id+"F0.wireOp",EDGE,"E13");Q6=makeQuery(id+"F7.opBoolean","SPLIT",EDGE,{"disambiguationData":[TD([makeQuery(id+"F5.opRevolve","CAP_FACE",FACE,{"disambiguationData":[OSD([subQ6,subQ5,subQ0,subQ4,subQ3,subQ2])],"isStart":false})])],"derivedFrom":makeQuery(id+"F1.opRevolve","SWEPT_EDGE",EDGE,{"disambiguationData":[OSD([subQ8,subQ7])]})});}
            var Q7;
            {var subQ0=sQuery(id+"F4.wireOp",EDGE,"E27");var subQ2=sQuery(id+"F4.wireOp",EDGE,"E30");var subQ3=sQuery(id+"F4.wireOp",EDGE,"E29");var subQ4=sQuery(id+"F4.wireOp",EDGE,"E28");var subQ5=sQuery(id+"F4.wireOp",EDGE,"E26");var subQ6=sQuery(id+"F4.wireOp",EDGE,"E25");var subQ7=sQuery(id+"F0.wireOp",EDGE,"E14");var subQ8=sQuery(id+"F0.wireOp",EDGE,"E13");Q7=makeQuery(id+"F7.opBoolean","SPLIT",EDGE,{"disambiguationData":[TD([makeQuery(id+"F6.opPattern","COPY",FACE,{"derivedFrom":makeQuery(id+"F5.opRevolve","CAP_FACE",FACE,{"disambiguationData":[OSD([subQ6,subQ5,subQ0,subQ4,subQ3,subQ2])],"isStart":true}),"instanceName":"6"})])],"derivedFrom":makeQuery(id+"F1.opRevolve","SWEPT_EDGE",EDGE,{"disambiguationData":[OSD([subQ8,subQ7])]})});}
            fillet(context, id + "F13", {"entities" : qUnion([Q0, Q1, Q2, Q3, Q4, Q5, Q6, Q7]), "radius" : .4 * mm, "tangentPropagation" : true, "allowEdgeOverflow" : false});
        }
        {
            var Q0;
            {var subQ0=sQuery(id+"F0.wireOp",EDGE,"E19");var subQ1=sQuery(id+"F0.wireOp",EDGE,"E20.trimOffspring");var subQ2=sQuery(id+"F4.wireOp",EDGE,"E30");var subQ3=sQuery(id+"F4.wireOp",EDGE,"E29");var subQ4=sQuery(id+"F4.wireOp",EDGE,"E28");var subQ5=sQuery(id+"F4.wireOp",EDGE,"E27");var subQ6=sQuery(id+"F4.wireOp",EDGE,"E26");var subQ7=sQuery(id+"F4.wireOp",EDGE,"E25");Q0=makeQuery(id+"F7.opBoolean","SPLIT",EDGE,{"disambiguationData":[TD([makeQuery(id+"F6.opPattern","COPY",FACE,{"derivedFrom":makeQuery(id+"F5.opRevolve","CAP_FACE",FACE,{"disambiguationData":[OSD([subQ7,subQ6,subQ5,subQ4,subQ3,subQ2])],"isStart":true}),"instanceName":"1"})])],"derivedFrom":makeQuery(id+"F1.opRevolve","SWEPT_EDGE",EDGE,{"disambiguationData":[OSD([subQ0,subQ1])]})});}
            var Q1;
            {var subQ0=sQuery(id+"F0.wireOp",EDGE,"E19");var subQ1=sQuery(id+"F0.wireOp",EDGE,"E20.trimOffspring");var subQ2=sQuery(id+"F4.wireOp",EDGE,"E30");var subQ3=sQuery(id+"F4.wireOp",EDGE,"E29");var subQ4=sQuery(id+"F4.wireOp",EDGE,"E28");var subQ5=sQuery(id+"F4.wireOp",EDGE,"E27");var subQ6=sQuery(id+"F4.wireOp",EDGE,"E26");var subQ7=sQuery(id+"F4.wireOp",EDGE,"E25");Q1=makeQuery(id+"F7.opBoolean","SPLIT",EDGE,{"disambiguationData":[TD([makeQuery(id+"F5.opRevolve","CAP_FACE",FACE,{"disambiguationData":[OSD([subQ7,subQ6,subQ5,subQ4,subQ3,subQ2])],"isStart":true})])],"derivedFrom":makeQuery(id+"F1.opRevolve","SWEPT_EDGE",EDGE,{"disambiguationData":[OSD([subQ0,subQ1])]})});}
            var Q2;
            {var subQ0=sQuery(id+"F0.wireOp",EDGE,"E19");var subQ1=sQuery(id+"F4.wireOp",EDGE,"E30");var subQ2=sQuery(id+"F4.wireOp",EDGE,"E29");var subQ3=sQuery(id+"F4.wireOp",EDGE,"E28");var subQ4=sQuery(id+"F4.wireOp",EDGE,"E27");var subQ5=sQuery(id+"F4.wireOp",EDGE,"E26");var subQ6=sQuery(id+"F4.wireOp",EDGE,"E25");var subQ7=sQuery(id+"F0.wireOp",EDGE,"E20.trimOffspring");Q2=makeQuery(id+"F7.opBoolean","SPLIT",EDGE,{"disambiguationData":[TD([makeQuery(id+"F5.opRevolve","CAP_FACE",FACE,{"disambiguationData":[OSD([subQ6,subQ5,subQ4,subQ3,subQ2,subQ1])],"isStart":false})])],"derivedFrom":makeQuery(id+"F1.opRevolve","SWEPT_EDGE",EDGE,{"disambiguationData":[OSD([subQ0,subQ7])]})});}
            var Q3;
            {var subQ0=sQuery(id+"F0.wireOp",EDGE,"E19");var subQ1=sQuery(id+"F0.wireOp",EDGE,"E20.trimOffspring");var subQ2=sQuery(id+"F4.wireOp",EDGE,"E30");var subQ3=sQuery(id+"F4.wireOp",EDGE,"E29");var subQ4=sQuery(id+"F4.wireOp",EDGE,"E28");var subQ5=sQuery(id+"F4.wireOp",EDGE,"E27");var subQ6=sQuery(id+"F4.wireOp",EDGE,"E26");var subQ7=sQuery(id+"F4.wireOp",EDGE,"E25");Q3=makeQuery(id+"F7.opBoolean","SPLIT",EDGE,{"disambiguationData":[TD([makeQuery(id+"F6.opPattern","COPY",FACE,{"derivedFrom":makeQuery(id+"F5.opRevolve","CAP_FACE",FACE,{"disambiguationData":[OSD([subQ7,subQ6,subQ5,subQ4,subQ3,subQ2])],"isStart":true}),"instanceName":"6"})])],"derivedFrom":makeQuery(id+"F1.opRevolve","SWEPT_EDGE",EDGE,{"disambiguationData":[OSD([subQ0,subQ1])]})});}
            var Q4;
            {var subQ0=sQuery(id+"F0.wireOp",EDGE,"E19");var subQ1=sQuery(id+"F0.wireOp",EDGE,"E20.trimOffspring");var subQ2=sQuery(id+"F4.wireOp",EDGE,"E30");var subQ3=sQuery(id+"F4.wireOp",EDGE,"E29");var subQ4=sQuery(id+"F4.wireOp",EDGE,"E28");var subQ5=sQuery(id+"F4.wireOp",EDGE,"E27");var subQ6=sQuery(id+"F4.wireOp",EDGE,"E26");var subQ7=sQuery(id+"F4.wireOp",EDGE,"E25");Q4=makeQuery(id+"F7.opBoolean","SPLIT",EDGE,{"disambiguationData":[TD([makeQuery(id+"F6.opPattern","COPY",FACE,{"derivedFrom":makeQuery(id+"F5.opRevolve","CAP_FACE",FACE,{"disambiguationData":[OSD([subQ7,subQ6,subQ5,subQ4,subQ3,subQ2])],"isStart":true}),"instanceName":"5"})])],"derivedFrom":makeQuery(id+"F1.opRevolve","SWEPT_EDGE",EDGE,{"disambiguationData":[OSD([subQ0,subQ1])]})});}
            var Q5;
            {var subQ0=sQuery(id+"F0.wireOp",EDGE,"E19");var subQ1=sQuery(id+"F4.wireOp",EDGE,"E30");var subQ2=sQuery(id+"F4.wireOp",EDGE,"E29");var subQ3=sQuery(id+"F4.wireOp",EDGE,"E28");var subQ4=sQuery(id+"F4.wireOp",EDGE,"E27");var subQ5=sQuery(id+"F4.wireOp",EDGE,"E26");var subQ6=sQuery(id+"F4.wireOp",EDGE,"E25");var subQ7=sQuery(id+"F0.wireOp",EDGE,"E20.trimOffspring");Q5=makeQuery(id+"F7.opBoolean","SPLIT",EDGE,{"disambiguationData":[TD([makeQuery(id+"F6.opPattern","COPY",FACE,{"derivedFrom":makeQuery(id+"F5.opRevolve","CAP_FACE",FACE,{"disambiguationData":[OSD([subQ6,subQ5,subQ4,subQ3,subQ2,subQ1])],"isStart":true}),"instanceName":"3"})])],"derivedFrom":makeQuery(id+"F1.opRevolve","SWEPT_EDGE",EDGE,{"disambiguationData":[OSD([subQ0,subQ7])]})});}
            var Q6;
            {var subQ0=sQuery(id+"F0.wireOp",EDGE,"E19");var subQ1=sQuery(id+"F0.wireOp",EDGE,"E20.trimOffspring");var subQ2=sQuery(id+"F4.wireOp",EDGE,"E30");var subQ3=sQuery(id+"F4.wireOp",EDGE,"E29");var subQ4=sQuery(id+"F4.wireOp",EDGE,"E28");var subQ5=sQuery(id+"F4.wireOp",EDGE,"E27");var subQ6=sQuery(id+"F4.wireOp",EDGE,"E26");var subQ7=sQuery(id+"F4.wireOp",EDGE,"E25");Q6=makeQuery(id+"F7.opBoolean","SPLIT",EDGE,{"disambiguationData":[TD([makeQuery(id+"F6.opPattern","COPY",FACE,{"derivedFrom":makeQuery(id+"F5.opRevolve","CAP_FACE",FACE,{"disambiguationData":[OSD([subQ7,subQ6,subQ5,subQ4,subQ3,subQ2])],"isStart":true}),"instanceName":"4"})])],"derivedFrom":makeQuery(id+"F1.opRevolve","SWEPT_EDGE",EDGE,{"disambiguationData":[OSD([subQ0,subQ1])]})});}
            var Q7;
            {var subQ0=sQuery(id+"F0.wireOp",EDGE,"E19");var subQ1=sQuery(id+"F4.wireOp",EDGE,"E30");var subQ2=sQuery(id+"F4.wireOp",EDGE,"E29");var subQ3=sQuery(id+"F4.wireOp",EDGE,"E28");var subQ4=sQuery(id+"F4.wireOp",EDGE,"E27");var subQ5=sQuery(id+"F4.wireOp",EDGE,"E26");var subQ6=sQuery(id+"F4.wireOp",EDGE,"E25");var subQ7=sQuery(id+"F0.wireOp",EDGE,"E20.trimOffspring");Q7=makeQuery(id+"F7.opBoolean","SPLIT",EDGE,{"disambiguationData":[TD([makeQuery(id+"F6.opPattern","COPY",FACE,{"derivedFrom":makeQuery(id+"F5.opRevolve","CAP_FACE",FACE,{"disambiguationData":[OSD([subQ6,subQ5,subQ4,subQ3,subQ2,subQ1])],"isStart":true}),"instanceName":"2"})])],"derivedFrom":makeQuery(id+"F1.opRevolve","SWEPT_EDGE",EDGE,{"disambiguationData":[OSD([subQ0,subQ7])]})});}
            fillet(context, id + "F14", {"entities" : qUnion([Q0, Q1, Q2, Q3, Q4, Q5, Q6, Q7]), "radius" : .5 * mm, "tangentPropagation" : true, "allowEdgeOverflow" : false});
        }
    });
